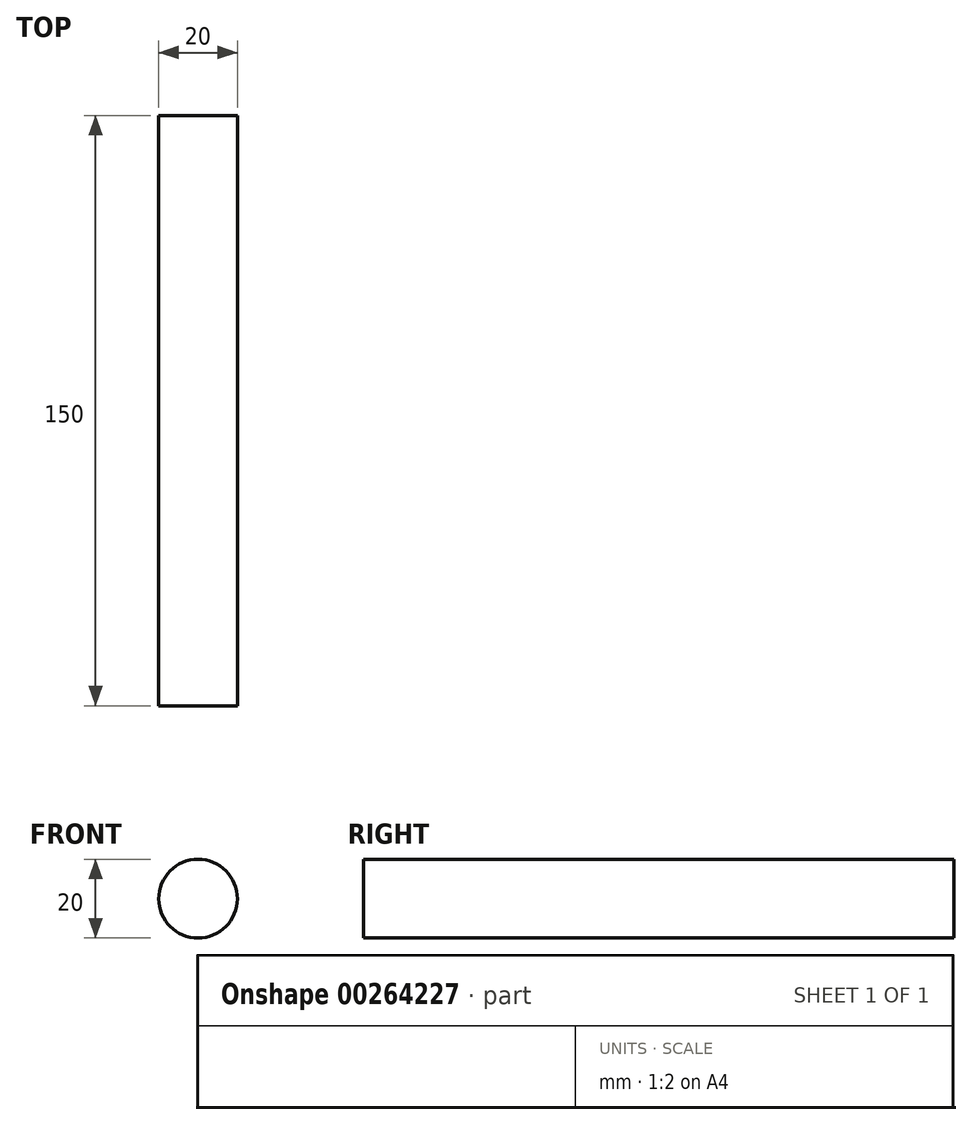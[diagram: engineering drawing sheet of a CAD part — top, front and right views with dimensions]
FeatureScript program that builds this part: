
annotation { "Feature Type Name" : "Feature", "Feature Type Description" : "" }
export const myFeature = defineFeature(function(context is Context, id is Id, definition is map)
    precondition{}
    {
        {
            var Q0;
            Q0=qCreatedBy(makeId("Front.planeOp"),FACE);
            var sketch = newSketch(context, id + "F0", { "sketchPlane" : qUnion([Q0])});
            skCircle(sketch, "E0", {"center": v(0, 0) * mm, "radius": 10 * mm});
            skSolve(sketch);
        }
        {
            var Q0;
            Q0 = qSketchRegion(id + "F0", true);
            extrude(context, id + "F1", {"entities" : qUnion([Q0]), "depth" : 25 * mm});
        }
        {
            var Q0;
            Q0=makeQuery(id+"F1.opExtrude","CAP_FACE",FACE,{"disambiguationData":[OSD([sQuery(id+"F0.wireOp",EDGE,"E0")])],"isStart":true});
            var Q1;
            Q1=makeQuery(id+"F1.opExtrude","CAP_FACE",FACE,{"disambiguationData":[OSD([sQuery(id+"F0.wireOp",EDGE,"E0")])],"isStart":false});
            extrude(context, id + "F2", {"entities" : qUnion([Q0, Q1]), "operationType" : NewBodyOperationType.ADD, "depth" : 25 * mm});
        }
        {
            var Q0;
            {var subQ0=sQuery(id+"F0.wireOp",EDGE,"E0");Q0=makeQuery(id+"F2.opExtrude","CAP_FACE",FACE,{"disambiguationData":[OSD([subQ0]),TDD([makeQuery(id+"F1.opExtrude","CAP_FACE",FACE,{"disambiguationData":[OSD([subQ0])],"isStart":true})])],"isStart":false});}
            extrude(context, id + "F3", {"entities" : qUnion([Q0]), "operationType" : NewBodyOperationType.ADD, "depth" : 100 * mm});
        }
    });
